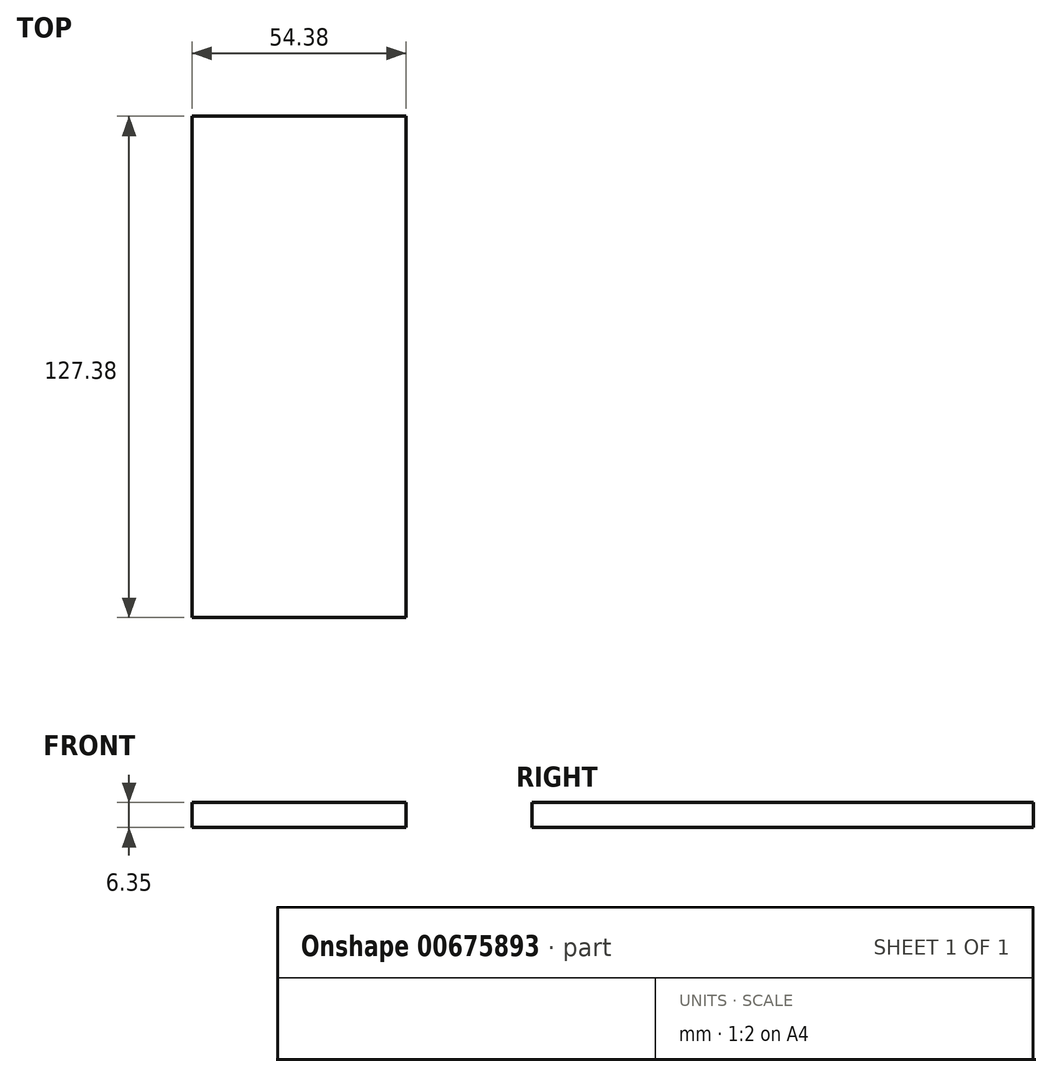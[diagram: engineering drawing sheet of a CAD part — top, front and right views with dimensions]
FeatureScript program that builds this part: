
annotation { "Feature Type Name" : "Feature", "Feature Type Description" : "" }
export const myFeature = defineFeature(function(context is Context, id is Id, definition is map)
    precondition{}
    {
        {
            var Q0;
            Q0=qCreatedBy(makeId("Top.planeOp"),FACE);
            var sketch = newSketch(context, id + "F0", { "sketchPlane" : qUnion([Q0])});
            skLineSegment(sketch, "E0.bottom", {"start": v(-27.2, 63.7) * mm, "end": v(27.2, 63.7) * mm});
            skLineSegment(sketch, "E0.top", {"start": v(-27.2, -63.7) * mm, "end": v(27.2, -63.7) * mm});
            skLineSegment(sketch, "E0.left", {"start": v(-27.2, 63.7) * mm, "end": v(-27.2, -63.7) * mm});
            skLineSegment(sketch, "E0.right", {"start": v(27.2, 63.7) * mm, "end": v(27.2, -63.7) * mm});
            skPoint(sketch, "E0.middle", {"position": v(0, 0) * mm});
            skSolve(sketch);
        }
        {
            var Q0;
            Q0 = qSketchRegion(id + "F0", true);
            extrude(context, id + "F1", {"entities" : qUnion([Q0]), "depth" : 6.35 * mm, "offsetDistance" : 25.4 * mm});
        }
    });
